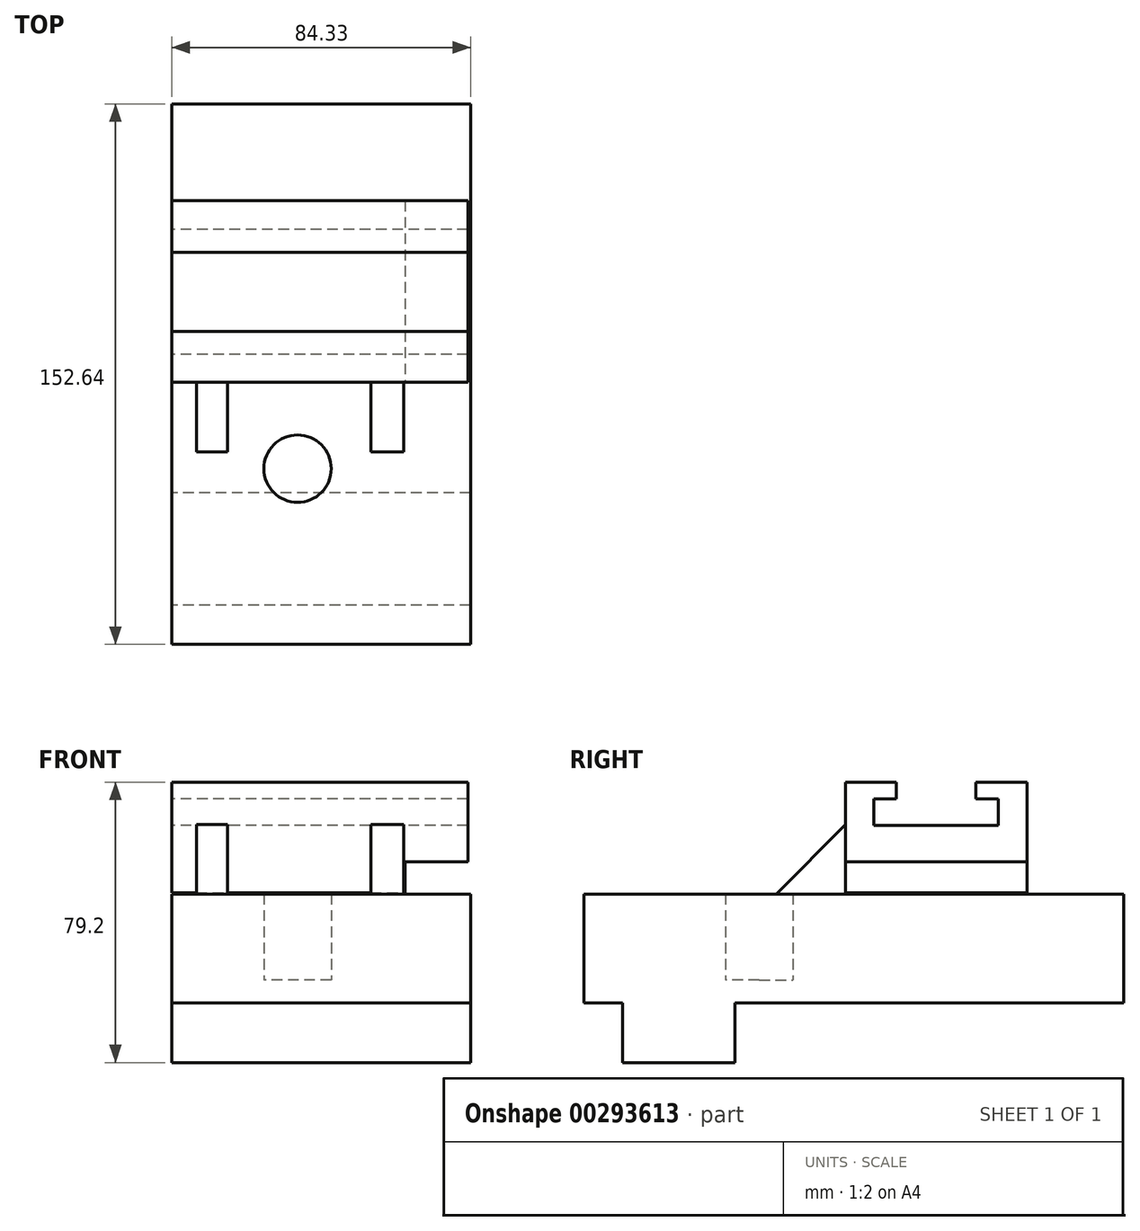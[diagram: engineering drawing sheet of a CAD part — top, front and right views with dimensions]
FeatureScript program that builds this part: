
annotation { "Feature Type Name" : "Feature", "Feature Type Description" : "" }
export const myFeature = defineFeature(function(context is Context, id is Id, definition is map)
    precondition{}
    {
        {
            var Q0;
            Q0=qCreatedBy(makeId("Right.planeOp"),FACE);
            var sketch = newSketch(context, id + "F0", { "sketchPlane" : qUnion([Q0])});
            skLineSegment(sketch, "E0", {"start": v(-74, 24.25) * mm, "end": v(-74, -6.58) * mm});
            skLineSegment(sketch, "E1", {"start": v(-74, -6.58) * mm, "end": v(-63, -6.58) * mm});
            skLineSegment(sketch, "E2", {"start": v(-63, -6.58) * mm, "end": v(-63, -23.38) * mm});
            skLineSegment(sketch, "E3", {"start": v(78.65, -6.58) * mm, "end": v(78.65, 24.25) * mm});
            skLineSegment(sketch, "E4", {"start": v(78.65, 24.25) * mm, "end": v(-74, 24.25) * mm});
            skLineSegment(sketch, "E5", {"start": v(-63, -23.38) * mm, "end": v(-31.25, -23.38) * mm});
            skLineSegment(sketch, "E6", {"start": v(-31.25, -23.38) * mm, "end": v(-31.25, -6.58) * mm});
            skLineSegment(sketch, "E7", {"start": v(-31.25, -6.58) * mm, "end": v(78.65, -6.58) * mm});
            skSolve(sketch);
        }
        {
            var Q0;
            Q0 = qSketchRegion(id + "F0", true);
            extrude(context, id + "F1", {"entities" : qUnion([Q0]), "depth" : 84.33 * mm});
        }
        {
            var Q0;
            Q0=qCreatedBy(makeId("Front.planeOp"),FACE);
            var sketch = newSketch(context, id + "F2", { "sketchPlane" : qUnion([Q0])});
            skLineSegment(sketch, "E8.bottom", {"start": v(6.9, 24.05) * mm, "end": v(15.64, 24.05) * mm});
            skLineSegment(sketch, "E8.top", {"start": v(6.9, 43.87) * mm, "end": v(15.64, 43.87) * mm});
            skLineSegment(sketch, "E8.left", {"start": v(6.9, 24.05) * mm, "end": v(6.9, 43.87) * mm});
            skLineSegment(sketch, "E8.right", {"start": v(15.64, 24.05) * mm, "end": v(15.64, 43.87) * mm});
            skLineSegment(sketch, "E9.bottom", {"start": v(56.16, 24.05) * mm, "end": v(65.48, 24.05) * mm});
            skLineSegment(sketch, "E9.top", {"start": v(56.16, 43.87) * mm, "end": v(65.48, 43.87) * mm});
            skLineSegment(sketch, "E9.left", {"start": v(56.16, 24.05) * mm, "end": v(56.16, 43.87) * mm});
            skLineSegment(sketch, "E9.right", {"start": v(65.48, 24.05) * mm, "end": v(65.48, 43.87) * mm});
            skSolve(sketch);
        }
        {
            var Q0;
            Q0 = qSketchRegion(id + "F2", true);
            extrude(context, id + "F3", {"entities" : qUnion([Q0]), "operationType" : NewBodyOperationType.ADD, "depth" : 25.4 * mm});
        }
        {
            var Q0;
            Q0=makeQuery(id+"F3.opExtrude","CAP_EDGE",EDGE,{"disambiguationData":[OSD([sQuery(id+"F2.wireOp",EDGE,"E8.top")])],"isStart":false});
            var Q1;
            Q1=makeQuery(id+"F3.opExtrude","CAP_EDGE",EDGE,{"disambiguationData":[OSD([sQuery(id+"F2.wireOp",EDGE,"E9.top")])],"isStart":false});
            chamfer(context, id + "F4", {"entities" : qUnion([Q0, Q1]), "width" : 25.4 * mm, "tangentPropagation" : true});
        }
        {
            var Q0;
            Q0=qCreatedBy(makeId("Top.planeOp"),FACE);
            var sketch = newSketch(context, id + "F5", { "sketchPlane" : qUnion([Q0])});
            skCircle(sketch, "E10", {"center": v(35.46, -24.4) * mm, "radius": 9.53 * mm});
            skSolve(sketch);
        }
        {
            var Q0;
            Q0 = qSketchRegion(id + "F5", true);
            extrude(context, id + "F6", {"entities" : qUnion([Q0]), "operationType" : NewBodyOperationType.REMOVE, "depth" : 36.83 * mm});
        }
        {
            var Q0;
            Q0=qCreatedBy(makeId("Front.planeOp"),FACE);
            var sketch = newSketch(context, id + "F7", { "sketchPlane" : qUnion([Q0])});
            skLineSegment(sketch, "E11", {"start": v(65.86, 33.37) * mm, "end": v(83.64, 33.37) * mm});
            skLineSegment(sketch, "E12", {"start": v(83.64, 33.37) * mm, "end": v(83.64, 55.82) * mm});
            skLineSegment(sketch, "E13", {"start": v(83.64, 55.82) * mm, "end": v(0, 55.82) * mm});
            skLineSegment(sketch, "E14", {"start": v(0, 55.82) * mm, "end": v(0, 24.63) * mm});
            skLineSegment(sketch, "E15", {"start": v(0, 24.63) * mm, "end": v(65.86, 24.63) * mm});
            skLineSegment(sketch, "E16", {"start": v(65.86, 24.63) * mm, "end": v(65.86, 33.37) * mm});
            skSolve(sketch);
        }
        {
            var Q0;
            Q0 = qSketchRegion(id + "F7", true);
            extrude(context, id + "F8", {"entities" : qUnion([Q0]), "operationType" : NewBodyOperationType.ADD, "oppositeDirection" : true, "depth" : 51.3 * mm});
        }
        {
            var Q0;
            Q0=qCreatedBy(makeId("Right.planeOp"),FACE);
            var sketch = newSketch(context, id + "F9", { "sketchPlane" : qUnion([Q0])});
            skLineSegment(sketch, "E17", {"start": v(14.34, 56.1) * mm, "end": v(14.34, 51.15) * mm});
            skLineSegment(sketch, "E18", {"start": v(14.34, 51.15) * mm, "end": v(7.93, 51.15) * mm});
            skLineSegment(sketch, "E19", {"start": v(36.79, 56.1) * mm, "end": v(36.79, 51.15) * mm});
            skLineSegment(sketch, "E20", {"start": v(36.79, 51.15) * mm, "end": v(43.2, 51.15) * mm});
            skLineSegment(sketch, "E21", {"start": v(14.34, 56.1) * mm, "end": v(36.79, 56.1) * mm});
            skLineSegment(sketch, "E22", {"start": v(43.2, 51.15) * mm, "end": v(43.2, 43.58) * mm});
            skLineSegment(sketch, "E23", {"start": v(43.2, 43.58) * mm, "end": v(7.93, 43.58) * mm});
            skLineSegment(sketch, "E24", {"start": v(7.93, 43.58) * mm, "end": v(7.93, 51.15) * mm});
            skSolve(sketch);
        }
        {
            var Q0;
            Q0 = qSketchRegion(id + "F9", true);
            extrude(context, id + "F10", {"entities" : qUnion([Q0]), "operationType" : NewBodyOperationType.REMOVE, "depth" : 88.9 * mm});
        }
    });
